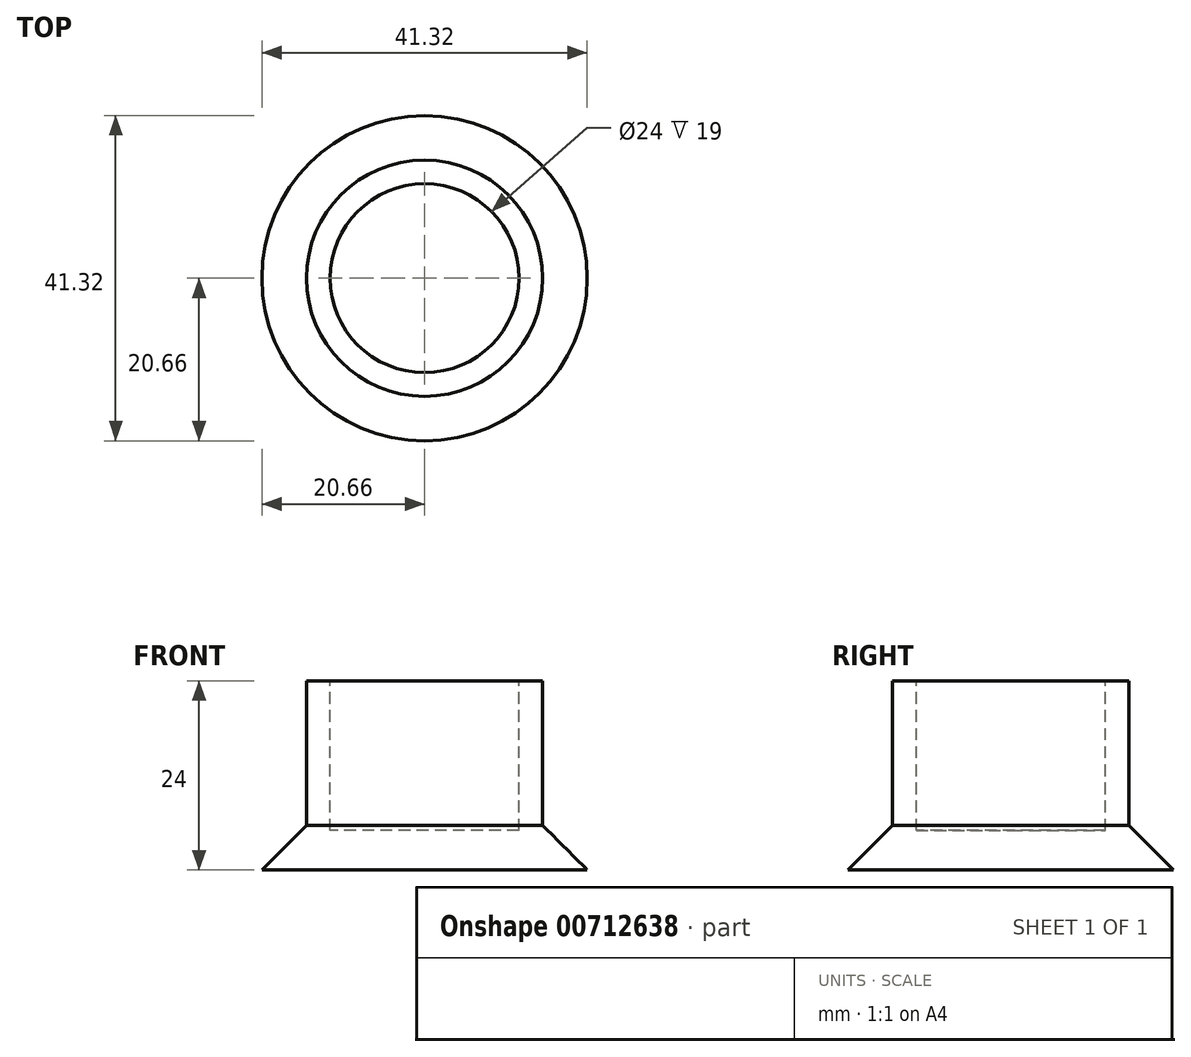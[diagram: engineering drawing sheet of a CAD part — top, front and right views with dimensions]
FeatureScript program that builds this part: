
annotation { "Feature Type Name" : "Feature", "Feature Type Description" : "" }
export const myFeature = defineFeature(function(context is Context, id is Id, definition is map)
    precondition{}
    {
        {
            var Q0;
            Q0=qCreatedBy(makeId("Front.planeOp"),FACE);
            var sketch = newSketch(context, id + "F0", { "sketchPlane" : qUnion([Q0])});
            skLineSegment(sketch, "E0", {"start": v(0, 0) * mm, "end": v(20.66, 0) * mm});
            skLineSegment(sketch, "E1", {"start": v(20.66, 0) * mm, "end": v(15, 5.66) * mm});
            skLineSegment(sketch, "E2", {"start": v(15, 5.66) * mm, "end": v(15, 24) * mm});
            skLineSegment(sketch, "E3", {"start": v(15, 24) * mm, "end": v(0, 24) * mm});
            skLineSegment(sketch, "E4", {"start": v(0, 24) * mm, "end": v(0, 0) * mm});
            skSolve(sketch);
        }
        {
            var Q0;
            Q0 = qSketchRegion(id + "F0", true);
            var Q1;
            Q1=sQuery(id+"F0.wireOp",EDGE,"E4");
            revolve(context, id + "F1", {"surfaceOperationType" : NewSurfaceOperationType.NEW, "entities" : qUnion([Q0]), "axis" : qUnion([Q1]), "revolveType" : RevolveType.FULL});
        }
        {
            var Q0;
            Q0=makeQuery(id+"F1.opRevolve","SWEPT_FACE",FACE,{"disambiguationData":[OSD([sQuery(id+"F0.wireOp",EDGE,"E3")])]});
            var sketch = newSketch(context, id + "F2", { "sketchPlane" : qUnion([Q0])});
            skCircle(sketch, "E5", {"center": v(0, 0) * mm, "radius": 12 * mm});
            skSolve(sketch);
        }
        {
            var Q0;
            Q0 = qSketchRegion(id + "F2", true);
            extrude(context, id + "F3", {"entities" : qUnion([Q0]), "operationType" : NewBodyOperationType.REMOVE, "oppositeDirection" : true, "depth" : 19 * mm, "offsetDistance" : 25 * mm});
        }
    });
